# Revit family: VIESSMANN - Energycal AW Pro MT DWS
name_source: partatom
category: Wyposażenie mechaniczne
revit_build: Autodesk Revit 2017 (Build: 20160720_1515(x64)
units: mm (PartAtom-declared; Revit-internal decimal feet)

## family parameters
Numer OmniClass = 23.75.10.21.11
Oparty na płaszczyźnie roboczej = Nie
Punkt obliczania pomieszczeń = Nie
Tnij formami wycięć po wczytaniu = Nie
Typ części = Normalny
Tytuł OmniClass = Air-Source Heat Pumps
Współdzielony = Nie
Wymiar okrągłego złącza = Użyj średnicy
Zawsze pionowo = Tak

## types (11) — shared parameters
Autor = www.archispace.pl
Częstotliwość = 50 Hz
Głębokość = 1208 mm  [stored 3.96325 ft]
Ilość/Obiegi chłodnicze sprężarki (nr/nr) = 2/2
Klasa efektywności (A7W45) = A
Liczba biegunów = 3
Moc nominalna silnika pompy obiegowej = 2 kW
Moc nominalna wentylatora = 2 kW
Model = Powietrzna pompa ciepła Energycal AW PRO MT / Air-water heat pump Energycal AW PRO MT DWS
Naczynie wzbiorcze = 18 m³
Napięcie zasilania = 400 V
Opis = Energycal AW Pro MT jest serią pomp ciepła o zakresie mocy od 94 do 244 kW w grupie R410A, z dwoma odrębnymi obiegami czynnika chłodniczego w celu zmaksymalizowania niezawodności.
Połączenia hydrauliczne = 2 1/2"
Producent = Viessmann Sp. z o.o
Prąd nominalny silnika pompy obiegowej = 5 A
Prąd nominalny wentylatora = 4 A
Stopień wydajności = 2
Typ sprężarki = Spiralna
Typ wentylatora = Osiowy
Typ wymiennika po stronie grzewczej = Płytowy
URL = https://www.viessmann-projektant.pl
Viessmann Kolor 1 = Viessmann Kolor 2
Viessmann Kolor 2 = Viessmann Kolor 3
Współczynnik mocy = 1
Wysokość = 1912 mm  [stored 6.27297 ft]
Zasilanie elektryczne (V/ph/Hz) = 400/3~/50+5%
Zasilanie pomocnicze (V/ph/Hz) = 230/1~/50+5%

## per-type parameters (varying)
- Wielkość jednostki - 95: Całkowite napełnienie czynnikiem chłodniczym=30.80 kg; Całkowite napełnienie olejem=5.40 kg; Ciężar transportowy=960.00 kg; Ciężar transportowy jednostki SLN=1167.00 kg; Ciężar w czasie pracy=966.00 kg; Ciężar w czasie pracy jednostki SLN=1175.00 kg; Długość=3508 mm  [stored 11.5092 ft]; Długość jednostki SLN=3508 mm  [stored 11.5092 ft]; Głębokość jednostki SLN=1208 mm  [stored 3.96325 ft]; Liczba wentylatorów=2; Maksymalna moc pobierania=39 kW; Maksymalny pobór prądu=68 A; Maksymalny prąd rozruchowy=214 A; Maksymalny prąd rozruchowy z układem Soft-Starter=128 A; Model pompy=P1; Natężenie przepływu wody (A7W45)=4.4 L/s; Natężenie przepływu wody (A7W45) l/h=15883; Nominalna moc grzewcza (A7W45)=94 kW; Nominalna moc pompy=2 kW; Obciążenie pozorne=39000 VA; Pobór mocy elektrycznej (A7W45)=28 kW; Pojemność wodna=6.2 m³; Pojemność zbiornika magazynowego=200 m³; Poziom ciśnienia akustycznego - wersja cicha LN dB(A)=54 mm  [stored 0.177165 ft]; Poziom ciśnienia akustycznego - wersja super cicha SLN dB(A)=51 mm; Poziom ciśnienia akustycznego dB(A)=56 mm  [stored 0.183727 ft]; Poziom mocy akustycznej - wersja cicha LN dB(A)=82 mm  [stored 0.269029 ft]; Poziom mocy akustycznej - wersja super cicha SLN dB(A)=79 mm; Poziom mocy akustycznej dB(A)=84 mm  [stored 0.275591 ft]; Przepływ powietrza=44000.0 m³/h; Robocza wysokość podnoszenia pompy (A7W45)=178.0 kPa; Spadek ciśnienia wody (A7W45)=41.0 kPa; TYP=AW PRO MT : AW PRO MT 95-160; Współczynnik efektywności [COP] (A7W45)=3.38; Wysokość jednostki SLN=1912 mm  [stored 6.27297 ft]
- Wielkość jednostki - 110: Całkowite napełnienie czynnikiem chłodniczym=36.30 kg; Całkowite napełnienie olejem=8.00 kg; Ciężar transportowy=1103.00 kg; Ciężar transportowy jednostki SLN=1365.00 kg; Ciężar w czasie pracy=1110.00 kg; Ciężar w czasie pracy jednostki SLN=1374.00 kg; Długość=3508 mm  [stored 11.5092 ft]; Długość jednostki SLN=3508 mm  [stored 11.5092 ft]; Głębokość jednostki SLN=1208 mm  [stored 3.96325 ft]; Liczba wentylatorów=2; Maksymalna moc pobierania=47 kW; Maksymalny pobór prądu=82 A; Maksymalny prąd rozruchowy=248 A; Maksymalny prąd rozruchowy z układem Soft-Starter=149 A; Model pompy=P1; Natężenie przepływu wody (A7W45)=5.2 L/s; Natężenie przepływu wody (A7W45) l/h=18721; Nominalna moc grzewcza (A7W45)=110 kW; Nominalna moc pompy=2 kW; Obciążenie pozorne=47100 VA; Pobór mocy elektrycznej (A7W45)=33 kW; Pojemność wodna=7.3 m³; Pojemność zbiornika magazynowego=200 m³; Poziom ciśnienia akustycznego - wersja cicha LN dB(A)=54 mm  [stored 0.177165 ft]; Poziom ciśnienia akustycznego - wersja super cicha SLN dB(A)=51 mm; Poziom ciśnienia akustycznego dB(A)=56 mm  [stored 0.183727 ft]; Poziom mocy akustycznej - wersja cicha LN dB(A)=82 mm  [stored 0.269029 ft]; Poziom mocy akustycznej - wersja super cicha SLN dB(A)=79 mm; Poziom mocy akustycznej dB(A)=84 mm  [stored 0.275591 ft]; Przepływ powietrza=44000.0 m³/h; Robocza wysokość podnoszenia pompy (A7W45)=164.0 kPa; Spadek ciśnienia wody (A7W45)=44.0 kPa; TYP=AW PRO MT : AW PRO MT 95-160; Współczynnik efektywności [COP] (A7W45)=3.3; Wysokość jednostki SLN=1912 mm  [stored 6.27297 ft]
- Wielkość jednostki - 130: Całkowite napełnienie czynnikiem chłodniczym=41.80 kg; Całkowite napełnienie olejem=10.60 kg; Ciężar transportowy=1167.00 kg; Ciężar transportowy jednostki SLN=1380.00 kg; Ciężar w czasie pracy=1175.00 kg; Ciężar w czasie pracy jednostki SLN=1390.00 kg; Długość=3508 mm  [stored 11.5092 ft]; Długość jednostki SLN=3508 mm  [stored 11.5092 ft]; Głębokość jednostki SLN=1208 mm  [stored 3.96325 ft]; Liczba wentylatorów=2; Maksymalna moc pobierania=55 kW; Maksymalny pobór prądu=82 A; Maksymalny prąd rozruchowy=248 A; Maksymalny prąd rozruchowy z układem Soft-Starter=149 A; Model pompy=P1; Natężenie przepływu wody (A7W45)=6.0 L/s; Natężenie przepływu wody (A7W45) l/h=21560; Nominalna moc grzewcza (A7W45)=127 kW; Nominalna moc pompy=2 kW; Obciążenie pozorne=55200 VA; Pobór mocy elektrycznej (A7W45)=39 kW; Pojemność wodna=8.4 m³; Pojemność zbiornika magazynowego=200 m³; Poziom ciśnienia akustycznego - wersja cicha LN dB(A)=54 mm  [stored 0.177165 ft]; Poziom ciśnienia akustycznego - wersja super cicha SLN dB(A)=51 mm; Poziom ciśnienia akustycznego dB(A)=56 mm  [stored 0.183727 ft]; Poziom mocy akustycznej - wersja cicha LN dB(A)=82 mm  [stored 0.269029 ft]; Poziom mocy akustycznej - wersja super cicha SLN dB(A)=79 mm; Poziom mocy akustycznej dB(A)=84 mm  [stored 0.275591 ft]; Przepływ powietrza=44000.0 m³/h; Robocza wysokość podnoszenia pompy (A7W45)=152.0 kPa; Spadek ciśnienia wody (A7W45)=43.0 kPa; TYP=AW PRO MT : AW PRO MT 95-160; Współczynnik efektywności [COP] (A7W45)=3.25; Wysokość jednostki SLN=1912 mm  [stored 6.27297 ft]
- Wielkość jednostki - 145: Całkowite napełnienie czynnikiem chłodniczym=46.40 kg; Całkowite napełnienie olejem=10.60 kg; Ciężar transportowy=1365.00 kg; Ciężar transportowy jednostki SLN=1585.00 kg; Ciężar w czasie pracy=1374.00 kg; Ciężar w czasie pracy jednostki SLN=1597.00 kg; Długość=3508 mm  [stored 11.5092 ft]; Długość jednostki SLN=4608 mm  [stored 15.1181 ft]; Głębokość jednostki SLN=1208 mm  [stored 3.96325 ft]; Liczba wentylatorów=2; Maksymalna moc pobierania=61 kW; Maksymalny pobór prądu=105 A; Maksymalny prąd rozruchowy=262 A; Maksymalny prąd rozruchowy z układem Soft-Starter=157 A; Model pompy=P1; Natężenie przepływu wody (A7W45)=6.7 L/s; Natężenie przepływu wody (A7W45) l/h=23961; Nominalna moc grzewcza (A7W45)=141 kW; Nominalna moc pompy=2 kW; Obciążenie pozorne=61200 VA; Pobór mocy elektrycznej (A7W45)=43 kW; Pojemność wodna=9.3 m³; Pojemność zbiornika magazynowego=200 m³; Poziom ciśnienia akustycznego - wersja cicha LN dB(A)=54 mm  [stored 0.177165 ft]; Poziom ciśnienia akustycznego - wersja super cicha SLN dB(A)=51 mm; Poziom ciśnienia akustycznego dB(A)=56 mm  [stored 0.183727 ft]; Poziom mocy akustycznej - wersja cicha LN dB(A)=82 mm  [stored 0.269029 ft]; Poziom mocy akustycznej - wersja super cicha SLN dB(A)=79 mm; Poziom mocy akustycznej dB(A)=84 mm  [stored 0.275591 ft]; Przepływ powietrza=44000.0 m³/h; Robocza wysokość podnoszenia pompy (A7W45)=138.0 kPa; Spadek ciśnienia wody (A7W45)=44.0 kPa; TYP=AW PRO MT : AW PRO MT 95-160; Współczynnik efektywności [COP] (A7W45)=3.31; Wysokość jednostki SLN=1912 mm  [stored 6.27297 ft]
- Wielkość jednostki - 160: Całkowite napełnienie czynnikiem chłodniczym=51.10 kg; Całkowite napełnienie olejem=10.60 kg; Ciężar transportowy=1380.00 kg; Ciężar transportowy jednostki SLN=1600.00 kg; Ciężar w czasie pracy=1390.00 kg; Ciężar w czasie pracy jednostki SLN=1613.00 kg; Długość=3508 mm  [stored 11.5092 ft]; Długość jednostki SLN=4608 mm  [stored 15.1181 ft]; Głębokość jednostki SLN=1208 mm  [stored 3.96325 ft]; Liczba wentylatorów=2; Maksymalna moc pobierania=67 kW; Maksymalny pobór prądu=114 A; Maksymalny prąd rozruchowy=218 A; Maksymalny prąd rozruchowy z układem Soft-Starter=131 A; Model pompy=P1; Natężenie przepływu wody (A7W45)=7.3 L/s; Natężenie przepływu wody (A7W45) l/h=26363; Nominalna moc grzewcza (A7W45)=155 kW; Nominalna moc pompy=2 kW; Obciążenie pozorne=67200 VA; Pobór mocy elektrycznej (A7W45)=46 kW; Pojemność wodna=10.2 m³; Pojemność zbiornika magazynowego=200 m³; Poziom ciśnienia akustycznego - wersja cicha LN dB(A)=54 mm  [stored 0.177165 ft]; Poziom ciśnienia akustycznego - wersja super cicha SLN dB(A)=51 mm; Poziom ciśnienia akustycznego dB(A)=56 mm  [stored 0.183727 ft]; Poziom mocy akustycznej - wersja cicha LN dB(A)=82 mm  [stored 0.269029 ft]; Poziom mocy akustycznej - wersja super cicha SLN dB(A)=79 mm; Poziom mocy akustycznej dB(A)=84 mm  [stored 0.275591 ft]; Przepływ powietrza=44000.0 m³/h; Robocza wysokość podnoszenia pompy (A7W45)=126.0 kPa; Spadek ciśnienia wody (A7W45)=43.0 kPa; TYP=AW PRO MT : AW PRO MT 95-160; Współczynnik efektywności [COP] (A7W45)=3.36; Wysokość jednostki SLN=1912 mm  [stored 6.27297 ft]
- Wielkość jednostki - 180: Całkowite napełnienie czynnikiem chłodniczym=58.20 kg; Całkowite napełnienie olejem=10.60 kg; Ciężar transportowy=1585.00 kg; Ciężar transportowy jednostki SLN=1610.00 kg; Ciężar w czasie pracy=1597.00 kg; Ciężar w czasie pracy jednostki SLN=1624.00 kg; Długość=4608 mm  [stored 15.1181 ft]; Długość jednostki SLN=4608 mm  [stored 15.1181 ft]; Głębokość jednostki SLN=1208 mm  [stored 3.96325 ft]; Liczba wentylatorów=2; Maksymalna moc pobierania=76 kW; Maksymalny pobór prądu=131 A; Maksymalny prąd rozruchowy=352 A; Maksymalny prąd rozruchowy z układem Soft-Starter=211 A; Model pompy=P2; Natężenie przepływu wody (A7W45)=8.3 L/s; Natężenie przepływu wody (A7W45) l/h=30046; Nominalna moc grzewcza (A7W45)=176 kW; Nominalna moc pompy=2 kW; Obciążenie pozorne=75800 VA; Pobór mocy elektrycznej (A7W45)=53 kW; Pojemność wodna=11.6 m³; Pojemność zbiornika magazynowego=400 m³; Poziom ciśnienia akustycznego - wersja cicha LN dB(A)=56 mm  [stored 0.183727 ft]; Poziom ciśnienia akustycznego - wersja super cicha SLN dB(A)=53 mm  [stored 0.173885 ft]; Poziom ciśnienia akustycznego dB(A)=58 mm  [stored 0.190289 ft]; Poziom mocy akustycznej - wersja cicha LN dB(A)=84 mm  [stored 0.275591 ft]; Poziom mocy akustycznej - wersja super cicha SLN dB(A)=81 mm  [stored 0.265748 ft]; Poziom mocy akustycznej dB(A)=86 mm  [stored 0.282152 ft]; Przepływ powietrza=66000.0 m³/h; Robocza wysokość podnoszenia pompy (A7W45)=141.0 kPa; Spadek ciśnienia wody (A7W45)=45.0 kPa; TYP=AW PRO MT : AW PRO MT 180-220; Współczynnik efektywności [COP] (A7W45)=3.52; Wysokość jednostki SLN=1912 mm  [stored 6.27297 ft]
- Wielkość jednostki - 200: Całkowite napełnienie czynnikiem chłodniczym=65.40 kg; Całkowite napełnienie olejem=10.60 kg; Ciężar transportowy=1600.00 kg; Ciężar transportowy jednostki SLN=1650.00 kg; Ciężar w czasie pracy=1613.00 kg; Ciężar w czasie pracy jednostki SLN=1664.00 kg; Długość=4608 mm  [stored 15.1181 ft]; Długość jednostki SLN=4608 mm  [stored 15.1181 ft]; Głębokość jednostki SLN=1208 mm  [stored 3.96325 ft]; Liczba wentylatorów=3; Maksymalna moc pobierania=83 kW; Maksymalny pobór prądu=144 A; Maksymalny prąd rozruchowy=365 A; Maksymalny prąd rozruchowy z układem Soft-Starter=219 A; Model pompy=P2; Natężenie przepływu wody (A7W45)=9.4 L/s; Natężenie przepływu wody (A7W45) l/h=33730; Nominalna moc grzewcza (A7W45)=198 kW; Nominalna moc pompy=2 kW; Obciążenie pozorne=82800 VA; Pobór mocy elektrycznej (A7W45)=58 kW; Pojemność wodna=13.1 m³; Pojemność zbiornika magazynowego=400 m³; Poziom ciśnienia akustycznego - wersja cicha LN dB(A)=56 mm  [stored 0.183727 ft]; Poziom ciśnienia akustycznego - wersja super cicha SLN dB(A)=53 mm  [stored 0.173885 ft]; Poziom ciśnienia akustycznego dB(A)=58 mm  [stored 0.190289 ft]; Poziom mocy akustycznej - wersja cicha LN dB(A)=84 mm  [stored 0.275591 ft]; Poziom mocy akustycznej - wersja super cicha SLN dB(A)=81 mm  [stored 0.265748 ft]; Poziom mocy akustycznej dB(A)=86 mm  [stored 0.282152 ft]; Przepływ powietrza=66000.0 m³/h; Robocza wysokość podnoszenia pompy (A7W45)=127.0 kPa; Spadek ciśnienia wody (A7W45)=43.0 kPa; TYP=AW PRO MT : AW PRO MT 180-220; Współczynnik efektywności [COP] (A7W45)=3.38; Wysokość jednostki SLN=1912 mm  [stored 6.27297 ft]
- Wielkość jednostki - 210: Całkowite napełnienie czynnikiem chłodniczym=68.60 kg; Całkowite napełnienie olejem=10.60 kg; Ciężar transportowy=1610.00 kg; Ciężar transportowy jednostki SLN=1820.00 kg; Ciężar w czasie pracy=1624.00 kg; Ciężar w czasie pracy jednostki SLN=1835.00 kg; Długość=4608 mm  [stored 15.1181 ft]; Długość jednostki SLN=5708 mm  [stored 18.727 ft]; Głębokość jednostki SLN=1208 mm  [stored 3.96325 ft]; Liczba wentylatorów=3; Maksymalna moc pobierania=88 kW; Maksymalny pobór prądu=154 A; Maksymalny prąd rozruchowy=365 A; Maksymalny prąd rozruchowy z układem Soft-Starter=219 A; Model pompy=P2; Natężenie przepływu wody (A7W45)=9.8 L/s; Natężenie przepływu wody (A7W45) l/h=35409; Nominalna moc grzewcza (A7W45)=207 kW; Nominalna moc pompy=2 kW; Obciążenie pozorne=87800 VA; Pobór mocy elektrycznej (A7W45)=62 kW; Pojemność wodna=13.7 m³; Pojemność zbiornika magazynowego=400 m³; Poziom ciśnienia akustycznego - wersja cicha LN dB(A)=56 mm  [stored 0.183727 ft]; Poziom ciśnienia akustycznego - wersja super cicha SLN dB(A)=53 mm  [stored 0.173885 ft]; Poziom ciśnienia akustycznego dB(A)=58 mm  [stored 0.190289 ft]; Poziom mocy akustycznej - wersja cicha LN dB(A)=84 mm  [stored 0.275591 ft]; Poziom mocy akustycznej - wersja super cicha SLN dB(A)=81 mm  [stored 0.265748 ft]; Poziom mocy akustycznej dB(A)=86 mm  [stored 0.282152 ft]; Przepływ powietrza=66000.0 m³/h; Robocza wysokość podnoszenia pompy (A7W45)=122.0 kPa; Spadek ciśnienia wody (A7W45)=41.0 kPa; TYP=AW PRO MT : AW PRO MT 180-220; Współczynnik efektywności [COP] (A7W45)=3.37; Wysokość jednostki SLN=1912 mm  [stored 6.27297 ft]
- Wielkość jednostki - 220: Całkowite napełnienie czynnikiem chłodniczym=71.90 kg; Całkowite napełnienie olejem=10.60 kg; Ciężar transportowy=1650.00 kg; Ciężar transportowy jednostki SLN=1870.00 kg; Ciężar w czasie pracy=1664.00 kg; Ciężar w czasie pracy jednostki SLN=1886.00 kg; Długość=4608 mm  [stored 15.1181 ft]; Długość jednostki SLN=5708 mm  [stored 18.727 ft]; Głębokość jednostki SLN=1208 mm  [stored 3.96325 ft]; Liczba wentylatorów=3; Maksymalna moc pobierania=93 kW; Maksymalny pobór prądu=164 A; Maksymalny prąd rozruchowy=355 A; Maksymalny prąd rozruchowy z układem Soft-Starter=213 A; Model pompy=P2; Natężenie przepływu wody (A7W45)=10.3 L/s; Natężenie przepływu wody (A7W45) l/h=37089; Nominalna moc grzewcza (A7W45)=217 kW; Nominalna moc pompy=2 kW; Obciążenie pozorne=92800 VA; Pobór mocy elektrycznej (A7W45)=65 kW; Pojemność wodna=14.4 m³; Pojemność zbiornika magazynowego=400 m³; Poziom ciśnienia akustycznego - wersja cicha LN dB(A)=56 mm  [stored 0.183727 ft]; Poziom ciśnienia akustycznego - wersja super cicha SLN dB(A)=53 mm  [stored 0.173885 ft]; Poziom ciśnienia akustycznego dB(A)=58 mm  [stored 0.190289 ft]; Poziom mocy akustycznej - wersja cicha LN dB(A)=84 mm  [stored 0.275591 ft]; Poziom mocy akustycznej - wersja super cicha SLN dB(A)=81 mm  [stored 0.265748 ft]; Poziom mocy akustycznej dB(A)=86 mm  [stored 0.282152 ft]; Przepływ powietrza=66000.0 m³/h; Robocza wysokość podnoszenia pompy (A7W45)=112.0 kPa; Spadek ciśnienia wody (A7W45)=43.0 kPa; TYP=AW PRO MT : AW PRO MT 180-220; Współczynnik efektywności [COP] (A7W45)=3.36; Wysokość jednostki SLN=1912 mm  [stored 6.27297 ft]
- Wielkość jednostki - 235: Całkowite napełnienie czynnikiem chłodniczym=76.30 kg; Całkowite napełnienie olejem=10.60 kg; Ciężar transportowy=1810.00 kg; Ciężar transportowy jednostki SLN=0.00 kg; Ciężar w czasie pracy=1835.00 kg; Ciężar w czasie pracy jednostki SLN=0.00 kg; Długość=5708 mm  [stored 18.727 ft]; Długość jednostki SLN=0 mm  [stored 0 ft]; Głębokość jednostki SLN=0 mm  [stored 0 ft]; Liczba wentylatorów=4; Maksymalna moc pobierania=93 kW; Maksymalny pobór prądu=164 A; Maksymalny prąd rozruchowy=355 A; Maksymalny prąd rozruchowy z układem Soft-Starter=213 A; Model pompy=P3; Natężenie przepływu wody (A7W45)=10.9 L/s; Natężenie przepływu wody (A7W45) l/h=39364; Nominalna moc grzewcza (A7W45)=230 kW; Nominalna moc pompy=3 kW; Obciążenie pozorne=92800 VA; Pobór mocy elektrycznej (A7W45)=69 kW; Pojemność wodna=15.3 m³; Pojemność zbiornika magazynowego=400 m³; Poziom ciśnienia akustycznego - wersja cicha LN dB(A)=59 mm; Poziom ciśnienia akustycznego - wersja super cicha SLN dB(A)=0 mm  [stored 0 ft]; Poziom ciśnienia akustycznego dB(A)=61 mm  [stored 0.200131 ft]; Poziom mocy akustycznej - wersja cicha LN dB(A)=87 mm  [stored 0.285433 ft]; Poziom mocy akustycznej - wersja super cicha SLN dB(A)=0 mm  [stored 0 ft]; Poziom mocy akustycznej dB(A)=89 mm  [stored 0.291995 ft]; Przepływ powietrza=88000.0 m³/h; Robocza wysokość podnoszenia pompy (A7W45)=151.0 kPa; Spadek ciśnienia wody (A7W45)=40.0 kPa; TYP=AW PRO MT : AW PRO MT 235-250; Współczynnik efektywności [COP] (A7W45)=3.34; Wysokość jednostki SLN=0 mm  [stored 0 ft]
- Wielkość jednostki - 250: Całkowite napełnienie czynnikiem chłodniczym=80.70 kg; Całkowite napełnienie olejem=10.60 kg; Ciężar transportowy=1810.00 kg; Ciężar transportowy jednostki SLN=0.00 kg; Ciężar w czasie pracy=1835.00 kg; Ciężar w czasie pracy jednostki SLN=0.00 kg; Długość=5708 mm  [stored 18.727 ft]; Długość jednostki SLN=0 mm  [stored 0 ft]; Głębokość jednostki SLN=0 mm  [stored 0 ft]; Liczba wentylatorów=4; Maksymalna moc pobierania=93 kW; Maksymalny pobór prądu=164 A; Maksymalny prąd rozruchowy=355 A; Maksymalny prąd rozruchowy z układem Soft-Starter=213 A; Model pompy=P3; Natężenie przepływu wody (A7W45)=11.6 L/s; Natężenie przepływu wody (A7W45) l/h=41639; Nominalna moc grzewcza (A7W45)=244 kW; Nominalna moc pompy=3 kW; Obciążenie pozorne=92800 VA; Pobór mocy elektrycznej (A7W45)=71 kW; Pojemność wodna=16.1 m³; Pojemność zbiornika magazynowego=400 m³; Poziom ciśnienia akustycznego - wersja cicha LN dB(A)=59 mm; Poziom ciśnienia akustycznego - wersja super cicha SLN dB(A)=0 mm  [stored 0 ft]; Poziom ciśnienia akustycznego dB(A)=61 mm  [stored 0.200131 ft]; Poziom mocy akustycznej - wersja cicha LN dB(A)=87 mm  [stored 0.285433 ft]; Poziom mocy akustycznej - wersja super cicha SLN dB(A)=0 mm  [stored 0 ft]; Poziom mocy akustycznej dB(A)=89 mm  [stored 0.291995 ft]; Przepływ powietrza=88000.0 m³/h; Robocza wysokość podnoszenia pompy (A7W45)=151.0 kPa; Spadek ciśnienia wody (A7W45)=43.0 kPa; TYP=AW PRO MT : AW PRO MT 235-250; Współczynnik efektywności [COP] (A7W45)=3.51; Wysokość jednostki SLN=0 mm  [stored 0 ft]

note: [stored X ft] marks values corroborated as IEEE doubles in the binary element streams (Revit-internal decimal feet)
